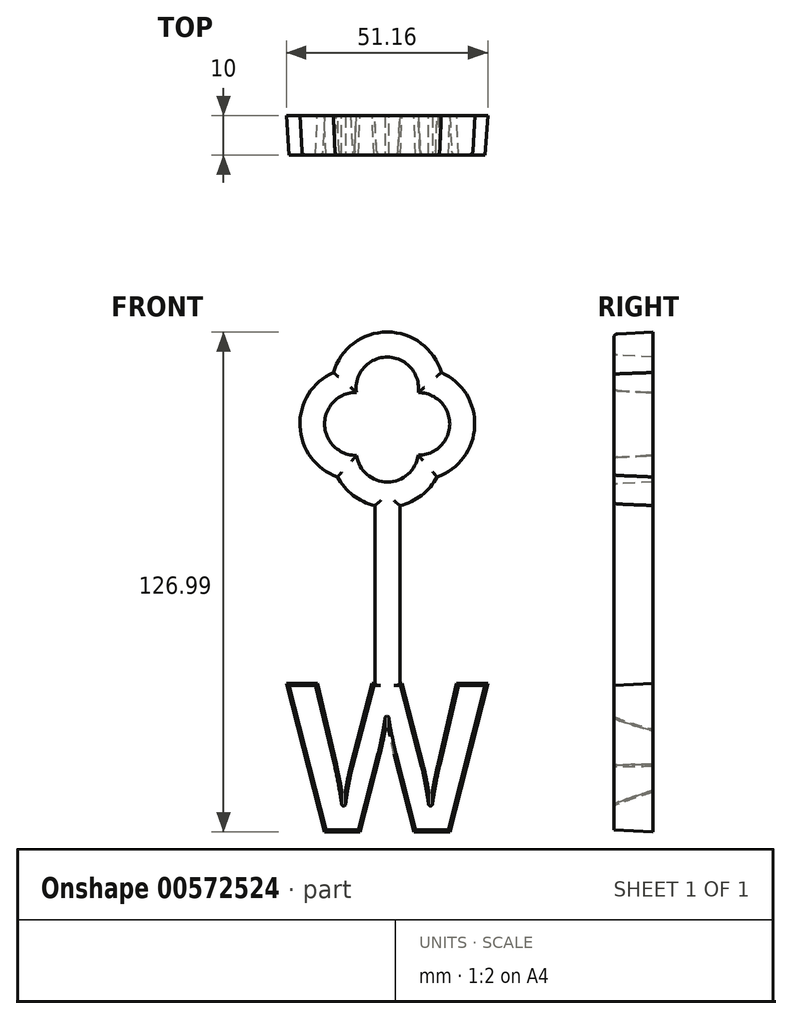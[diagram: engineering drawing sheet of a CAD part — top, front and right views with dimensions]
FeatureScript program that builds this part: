
annotation { "Feature Type Name" : "Feature", "Feature Type Description" : "" }
export const myFeature = defineFeature(function(context is Context, id is Id, definition is map)
    precondition{}
    {
        {
            var Q0;
            Q0=qCreatedBy(makeId("Front.planeOp"),FACE);
            var sketch = newSketch(context, id + "F0", { "sketchPlane" : qUnion([Q0])});
            skLineSegment(sketch, "E0", {"start": v(0, 48.17) * mm, "end": v(0, 48.17) * mm});
            skArc(sketch, "E1", {"start": v(-7.84, 40.16) * mm, "mid": v(0.04, 33.42) * mm, "end": v(7.85, 40.24) * mm});
            skArc(sketch, "E2", {"start": v(7.85, 40.24) * mm, "mid": v(15.86, 48.17) * mm, "end": v(7.85, 56.1) * mm});
            skArc(sketch, "E3", {"start": v(7.85, 56.1) * mm, "mid": v(0.04, 65.14) * mm, "end": v(-7.86, 56.17) * mm});
            skPoint(sketch, "E4.center.orphan", {"position": v(0, 48.17) * mm});
            skLineSegment(sketch, "E5", {"start": v(0, 49.28) * mm, "end": v(0, 49.28) * mm});
            skPoint(sketch, "E6.orphan", {"position": v(0, 61.28) * mm});
            skArc(sketch, "E7.trimOffspring", {"start": v(-7.86, 56.17) * mm, "mid": v(-15.94, 48.16) * mm, "end": v(-7.84, 40.16) * mm});
            skArc(sketch, "E8", {"start": v(-12.63, 34.68) * mm, "mid": v(0, 27.07) * mm, "end": v(12.63, 34.68) * mm});
            skArc(sketch, "E9", {"start": v(12.63, 34.68) * mm, "mid": v(22.2, 47.59) * mm, "end": v(13.7, 61.23) * mm});
            skArc(sketch, "E10", {"start": v(13.7, 61.23) * mm, "mid": v(0, 71.5) * mm, "end": v(-13.7, 61.23) * mm});
            skArc(sketch, "E11", {"start": v(-13.7, 61.23) * mm, "mid": v(-22.2, 47.59) * mm, "end": v(-12.63, 34.68) * mm});
            skLineSegment(sketch, "E12", {"start": v(-3.18, -23.06) * mm, "end": v(3.18, -23.06) * mm});
            skPoint(sketch, "E12.startSnap0", {"position": v(0, -23.06) * mm});
            skPoint(sketch, "E13.startSnap0", {"position": v(0.04, 33.42) * mm});
            skLineSegment(sketch, "E14", {"start": v(-3.18, -23.06) * mm, "end": v(-3.18, 34.08) * mm});
            skLineSegment(sketch, "E15", {"start": v(3.18, -23.06) * mm, "end": v(3.18, 34.08) * mm});
            skText(sketch, "E16", { "text": "W", "fontName": "NotoSans-Bold.ttf"});
            const initialGuessF0  = {"E16": [-0.02565, -0.0555, 1, 0, 0.0381]};
            skSetInitialGuess(sketch, initialGuessF0);
            skSolve(sketch);
        }
        {
            var Q0;
            Q0 = qSketchRegion(id + "F0", true);
            extrude(context, id + "F1", {"entities" : qUnion([Q0]), "depth" : 10 * mm, "offsetDistance" : 25 * mm, "hasDraft" : true, "draftAngle" : 3 * degree, "draftPullDirection" : true});
        }
        {
            var Q0;
            Q0=makeQuery(id+"F1.opExtrude","CAP_EDGE",EDGE,{"disambiguationData":[OSD([sQuery(id+"F0.wireOp",EDGE,"E14")])],"isStart":false});
            var Q1;
            Q1=makeQuery(id+"F1.opExtrude","CAP_EDGE",EDGE,{"disambiguationData":[OSD([sQuery(id+"F0.wireOp",EDGE,"E15")])],"isStart":false});
            var Q2;
            {var subQ0=sQuery(id+"F0.wireOp",EDGE,"E8");Q2=makeQuery(id+"F1.opExtrude","CAP_EDGE",EDGE,{"disambiguationData":[OSD([subQ0]),TDD([makeQuery(id+"F0.imprint","IMPRINT",EDGE,{"disambiguationData":[TD([[makeQuery(id+"F0.imprint","INTERSECT",VERTEX,{"derivedFrom":[subQ0,sQuery(id+"F0.wireOp",EDGE,"E11")]}),-1.0]])],"derivedFrom":subQ0})])],"isStart":false});}
            var Q3;
            {var subQ0=sQuery(id+"F0.wireOp",EDGE,"E8");Q3=makeQuery(id+"F1.opExtrude","CAP_EDGE",EDGE,{"disambiguationData":[OSD([subQ0]),TDD([makeQuery(id+"F0.imprint","IMPRINT",EDGE,{"disambiguationData":[TD([[makeQuery(id+"F0.imprint","INTERSECT",VERTEX,{"derivedFrom":[subQ0,sQuery(id+"F0.wireOp",EDGE,"E9")]}),1.0]])],"derivedFrom":subQ0})])],"isStart":false});}
            var Q4;
            Q4=makeQuery(id+"F1.opExtrude","CAP_EDGE",EDGE,{"disambiguationData":[OSD([sQuery(id+"F0.wireOp",EDGE,"E11")])],"isStart":false});
            var Q5;
            Q5=makeQuery(id+"F1.opExtrude","CAP_EDGE",EDGE,{"disambiguationData":[OSD([sQuery(id+"F0.wireOp",EDGE,"E7.trimOffspring")])],"isStart":false});
            var Q6;
            Q6=makeQuery(id+"F1.opExtrude","CAP_EDGE",EDGE,{"disambiguationData":[OSD([sQuery(id+"F0.wireOp",EDGE,"E1")])],"isStart":false});
            var Q7;
            Q7=makeQuery(id+"F1.opExtrude","CAP_EDGE",EDGE,{"disambiguationData":[OSD([sQuery(id+"F0.wireOp",EDGE,"E9")])],"isStart":false});
            var Q8;
            Q8=makeQuery(id+"F1.opExtrude","CAP_EDGE",EDGE,{"disambiguationData":[OSD([sQuery(id+"F0.wireOp",EDGE,"E2")])],"isStart":false});
            var Q9;
            Q9=makeQuery(id+"F1.opExtrude","CAP_EDGE",EDGE,{"disambiguationData":[OSD([sQuery(id+"F0.wireOp",EDGE,"E3")])],"isStart":false});
            var Q10;
            Q10=makeQuery(id+"F1.opExtrude","CAP_EDGE",EDGE,{"disambiguationData":[OSD([sQuery(id+"F0.wireOp",EDGE,"E10")])],"isStart":false});
            fillet(context, id + "F2", {"entities" : qUnion([Q0, Q1, Q2, Q3, Q4, Q5, Q6, Q7, Q8, Q9, Q10]), "radius" : 1 * mm, "tangentPropagation" : true, "allowEdgeOverflow" : false});
        }
        {
            var Q0;
            Q0=makeQuery(id+"F1.opExtrude","SWEPT_EDGE",EDGE,{"disambiguationData":[OSD([sQuery(id+"F0.wireOp",EDGE,"E16.sketch_text.stroke-11"),sQuery(id+"F0.wireOp",EDGE,"E16.sketch_text.stroke-12")])]});
            var Q1;
            Q1=makeQuery(id+"F1.opExtrude","SWEPT_EDGE",EDGE,{"disambiguationData":[OSD([sQuery(id+"F0.wireOp",EDGE,"E16.sketch_text.stroke-18"),sQuery(id+"F0.wireOp",EDGE,"E16.sketch_text.stroke-19")])]});
            var Q2;
            Q2=makeQuery(id+"F1.opExtrude","SWEPT_EDGE",EDGE,{"disambiguationData":[OSD([sQuery(id+"F0.wireOp",EDGE,"E16.sketch_text.stroke-3"),sQuery(id+"F0.wireOp",EDGE,"E16.sketch_text.stroke-4")])]});
            fillet(context, id + "F3", {"entities" : qUnion([Q0, Q1, Q2]), "radius" : 0.5 * mm, "tangentPropagation" : true, "allowEdgeOverflow" : false});
        }
    });
